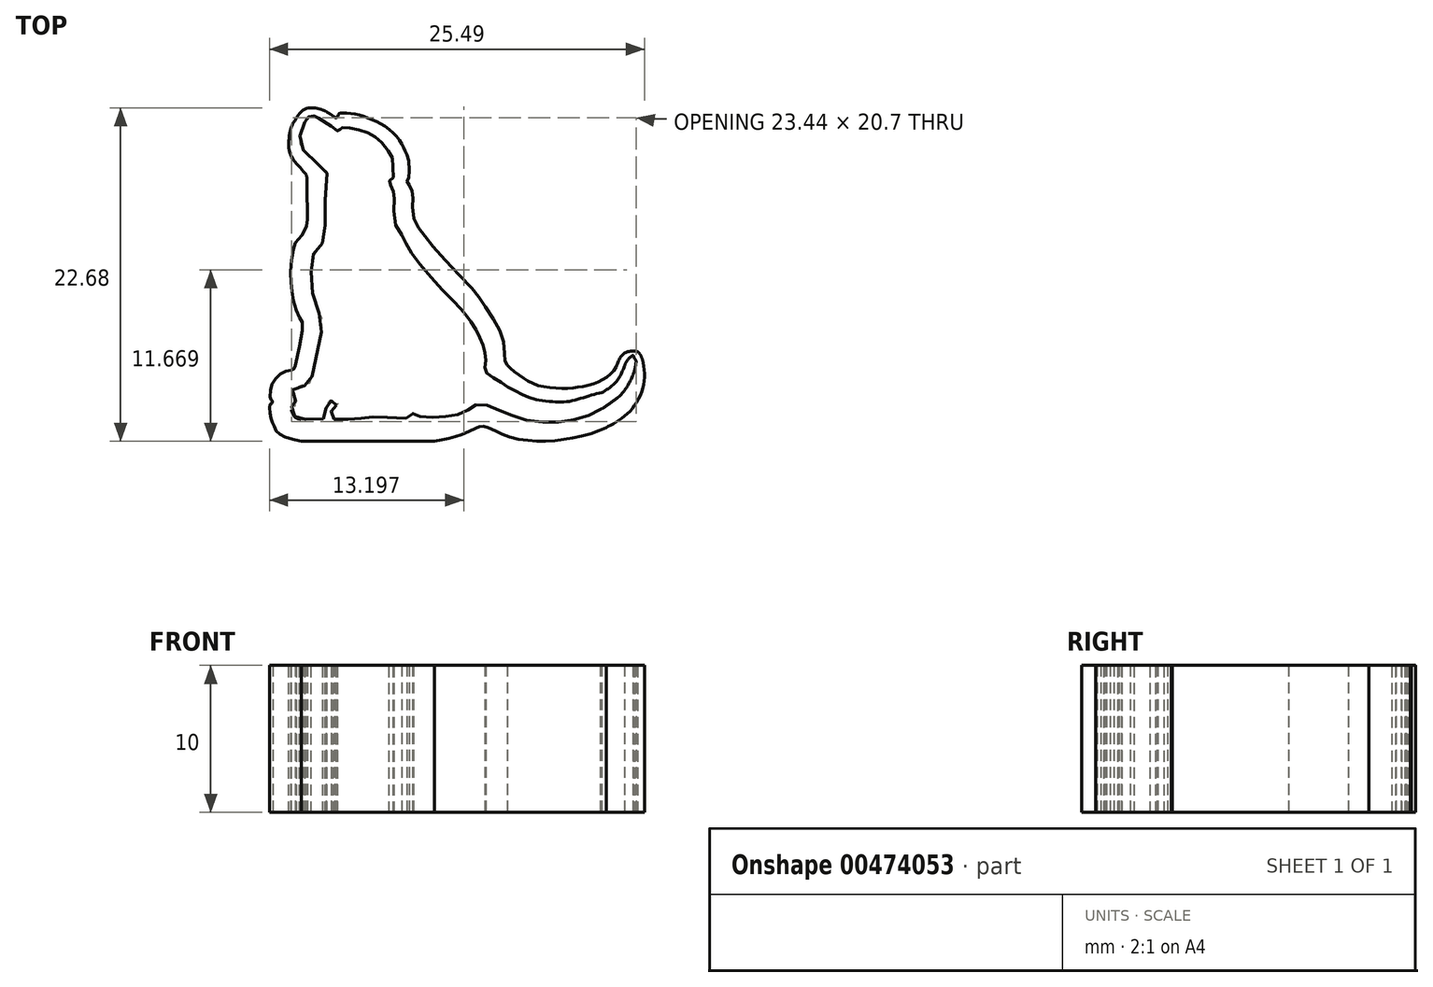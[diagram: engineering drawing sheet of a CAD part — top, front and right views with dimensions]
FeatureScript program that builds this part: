
annotation { "Feature Type Name" : "Feature", "Feature Type Description" : "" }
export const myFeature = defineFeature(function(context is Context, id is Id, definition is map)
    precondition{}
    {
        {
            var Q0;
            Q0=qCreatedBy(makeId("Top.planeOp"),FACE);
            var sketch = newSketch(context, id + "F0", { "sketchPlane" : qUnion([Q0])});
            skFitSpline(sketch, "E0", {"points": [v(-18.64, 26.8) * mm, v(-17.67, 25.17) * mm, v(-15, 22.17) * mm, v(-14.18, 21.25) * mm, v(-13.45, 20.1) * mm, v(-13.07, 19.16) * mm, v(-12.93, 18.19) * mm, v(-12.96, 17.55) * mm, v(-12.13, 16.92) * mm, v(-11.21, 16.35) * mm, v(-10.31, 15.9) * mm, v(-9.5, 15.6) * mm, v(-8.22, 15.45) * mm, v(-7.3, 15.48) * mm, v(-6.28, 15.74) * mm, v(-5.41, 16) * mm, v(-4.68, 16.04) * mm, v(-4.2, 15.74) * mm, v(-4.11, 15.31) * mm, v(-4.47, 14.84) * mm], "startDerivative": vector(10.05, -20.8) * mm, "endDerivative": vector(-11.78, -11.66) * mm});
            skFitSpline(sketch, "E1", {"points": [v(-9.5, 15.6) * mm, v(-8.72, 15.47) * mm, v(-7.72, 15.38) * mm, v(-6.88, 15.45) * mm, v(-6.21, 15.6) * mm, v(-5.62, 15.8) * mm, v(-5.06, 15.91) * mm, v(-4.74, 15.84) * mm, v(-4.58, 15.6) * mm, v(-4.64, 15.45) * mm, v(-4.81, 15.22) * mm, v(-5.13, 14.94) * mm, v(-5.65, 14.65) * mm, v(-6.3, 14.4) * mm, v(-7.1, 14.19) * mm, v(-7.82, 14.1) * mm, v(-8.74, 14.07) * mm, v(-9.5, 14.11) * mm, v(-10.51, 14.3) * mm, v(-11.1, 14.5) * mm, v(-11.64, 14.71) * mm, v(-12.33, 15) * mm, v(-12.8, 15.2) * mm, v(-13.18, 15.28) * mm, v(-13.65, 15.21) * mm, v(-13.89, 15.06) * mm, v(-14.13, 14.88) * mm, v(-14.44, 14.71) * mm, v(-14.94, 14.56) * mm, v(-15.47, 14.48) * mm, v(-16.02, 14.43) * mm, v(-16.6, 14.4) * mm, v(-17.18, 14.43) * mm, v(-17.55, 14.5) * mm, v(-17.68, 14.65) * mm, v(-17.88, 14.66) * mm, v(-17.96, 14.47) * mm, v(-18.17, 14.36) * mm, v(-19.22, 14.37) * mm, v(-20.18, 14.41) * mm, v(-20.7, 14.43) * mm, v(-21.2, 14.36) * mm, v(-21.69, 14.3) * mm, v(-22.28, 14.26) * mm, v(-23, 14.28) * mm, v(-23.35, 14.32) * mm, v(-23.43, 14.63) * mm, v(-23.4, 14.91) * mm, v(-23.24, 15.12) * mm, v(-23.07, 15.23) * mm], "startDerivative": vector(23.7, -7.27) * mm, "endDerivative": vector(13.55, 6.78) * mm});
            skFitSpline(sketch, "E2", {"points": [v(-18.64, 26.8) * mm, v(-19.13, 27.71) * mm, v(-19.15, 29.17) * mm, v(-19.16, 29.6) * mm, v(-19.26, 29.95) * mm, v(-19.43, 30.25) * mm, v(-19.49, 30.38) * mm, v(-19.43, 30.5) * mm, v(-19.26, 30.6) * mm, v(-19.2, 31.05) * mm, v(-19.26, 31.93) * mm, v(-19.33, 32.16) * mm, v(-19.82, 32.9) * mm, v(-20.2, 33.28) * mm, v(-20.67, 33.61) * mm, v(-21.2, 33.84) * mm, v(-21.83, 34.02) * mm, v(-22.38, 34.1) * mm, v(-22.69, 34.1) * mm, v(-22.78, 34.08) * mm, v(-22.83, 34) * mm, v(-22.85, 33.9) * mm, v(-22.92, 33.87) * mm, v(-23.02, 33.88) * mm, v(-23.16, 33.98) * mm, v(-24.31, 34.78) * mm, v(-24.49, 34.85) * mm, v(-24.67, 34.9) * mm, v(-24.86, 34.88) * mm, v(-25.01, 34.78) * mm, v(-25.2, 34.53) * mm, v(-25.25, 34.43) * mm, v(-25.24, 34.3) * mm, v(-25.23, 34.18) * mm], "startDerivative": vector(-11.38, 14.65) * mm, "endDerivative": vector(0.42, -6.75) * mm});
            skFitSpline(sketch, "E3", {"points": [v(-25.2, 34.53) * mm, v(-25.43, 34.12) * mm, v(-25.55, 33.7) * mm, v(-25.57, 33.14) * mm, v(-25.47, 32.8) * mm, v(-25.05, 32.28) * mm, v(-24.37, 31.64) * mm, v(-23.88, 31.24) * mm, v(-23.75, 31.13) * mm, v(-23.71, 30.96) * mm, v(-23.81, 29.43) * mm, v(-23.83, 27.82) * mm, v(-23.86, 27.12) * mm, v(-23.99, 26.36) * mm, v(-24.2, 26) * mm, v(-24.5, 25.67) * mm, v(-24.72, 25.34) * mm, v(-24.79, 24.67) * mm, v(-24.75, 23.66) * mm, v(-24.68, 22.74) * mm, v(-24.45, 21.84) * mm, v(-24.06, 21.1) * mm, v(-24.02, 20.72) * mm, v(-24.75, 17.1) * mm, v(-24.88, 16.75) * mm, v(-25.02, 16.6) * mm, v(-25.46, 16.55) * mm, v(-25.84, 16.43) * mm, v(-26.05, 16.28) * mm, v(-26.1, 15.69) * mm, v(-25.95, 15.55) * mm, v(-25.8, 15.44) * mm, v(-25.8, 15.29) * mm, v(-25.91, 15.22) * mm, v(-26.08, 15.2) * mm, v(-26.14, 14.98) * mm, v(-26.1, 14.74) * mm, v(-25.97, 14.52) * mm, v(-25.8, 14.35) * mm, v(-25.63, 14.29) * mm, v(-25.36, 14.27) * mm, v(-24.45, 14.27) * mm, v(-24.02, 14.29) * mm, v(-23.87, 14.38) * mm, v(-23.84, 14.72) * mm, v(-23.78, 15.01) * mm, v(-23.63, 15.25) * mm, v(-23.6, 15.46) * mm, v(-23.52, 15.52) * mm, v(-23.34, 15.52) * mm, v(-23.16, 15.45) * mm, v(-22.98, 15.35) * mm, v(-23.07, 15.23) * mm], "startDerivative": vector(-12.69, -20.47) * mm, "endDerivative": vector(-12.96, -11.1) * mm});
            skFitSpline(sketch, "E4", {"points": [v(-23.08, 16.7) * mm, v(-21.94, 19.17) * mm, v(-21.85, 19.47) * mm, v(-21.79, 19.58) * mm, v(-21.64, 19.6) * mm, v(-21.56, 19.53) * mm, v(-21.54, 19.42) * mm, v(-21.46, 19.35) * mm, v(-21.26, 19.2) * mm, v(-21.06, 19.1) * mm, v(-20.96, 19.02) * mm, v(-20.97, 18.84) * mm, v(-21.11, 18.68) * mm, v(-21.16, 18.5) * mm, v(-21.17, 18.18) * mm, v(-21.1, 17.9) * mm, v(-20.94, 17.57) * mm, v(-20.66, 17.12) * mm, v(-20.63, 16.86) * mm, v(-20.8, 16.71) * mm, v(-21.1, 16.62) * mm, v(-21.6, 16.57) * mm, v(-22.32, 16.56) * mm, v(-22.93, 16.5) * mm, v(-23.08, 16.53) * mm, v(-23.13, 16.58) * mm, v(-23.08, 16.7) * mm]});
            skFitSpline(sketch, "E5", {"points": [v(-21.86, 15.57) * mm, v(-19.82, 15.8) * mm, v(-19.69, 15.8) * mm, v(-19.62, 15.6) * mm, v(-19.68, 15.5) * mm, v(-20.03, 15.34) * mm, v(-20.57, 15.23) * mm, v(-21.23, 15.2) * mm, v(-21.7, 15.28) * mm, v(-21.84, 15.34) * mm], "startDerivative": vector(10.76, 1.04) * mm, "endDerivative": vector(-1.73, 0.9) * mm});
            skFitSpline(sketch, "E6", {"points": [v(-21.84, 15.34) * mm, v(-21.88, 15.44) * mm, v(-21.86, 15.57) * mm], "startDerivative": vector(-0.1, 0.21) * mm, "endDerivative": vector(0.07, 0.25) * mm});
            skPoint(sketch, "E7.1.internal.orphan", {"position": v(-24.41, 31.05) * mm});
            skPoint(sketch, "E8.7.internal.snap0", {"position": v(-11.42, 13.4) * mm});
            skPoint(sketch, "E8.8.internal.snap0", {"position": v(-11.42, 13.45) * mm});
            skFitSpline(sketch, "E9.trimOffspring", {"points": [v(-11.33, 13.53) * mm, v(-12.83, 14.23) * mm, v(-13.03, 14.3) * mm, v(-13.4, 14.32) * mm, v(-13.63, 14.24) * mm, v(-14.53, 13.84) * mm, v(-15.5, 13.53) * mm, v(-18.01, 13.4) * mm, v(-24.51, 13.45) * mm, v(-26.14, 14.16) * mm], "startDerivative": vector(-14.88, 6.54) * mm, "endDerivative": vector(-9.16, 7.25) * mm});
            skFitSpline(sketch, "E10.trimOffspring", {"points": [v(-25.27, 17.31) * mm, v(-25.4, 17.12) * mm, v(-25.87, 17.05) * mm, v(-26.28, 16.9) * mm, v(-26.59, 16.65) * mm, v(-26.82, 16.2) * mm, v(-26.85, 15.72) * mm, v(-26.81, 15.56) * mm, v(-26.7, 15.48) * mm, v(-26.7, 15.43) * mm, v(-26.72, 15.35) * mm, v(-26.78, 15.29) * mm, v(-26.81, 15.27) * mm, v(-26.83, 15.23) * mm, v(-26.84, 15.17) * mm, v(-26.79, 14.82) * mm, v(-26.75, 14.37) * mm, v(-26.31, 13.9) * mm, v(-24.51, 13.45) * mm], "startDerivative": vector(-1.67, -4.49) * mm, "endDerivative": vector(14.6, -2.5) * mm});
            skFitSpline(sketch, "E11", {"points": [v(-6.48, 17.1) * mm, v(-7.36, 16.99) * mm, v(-8.18, 16.99) * mm, v(-9.04, 17.07) * mm, v(-9.92, 17.26) * mm, v(-10.74, 17.6) * mm, v(-11.45, 17.93) * mm, v(-11.59, 18.15) * mm, v(-11.63, 18.41) * mm, v(-11.7, 19.47) * mm, v(-12.19, 20.74) * mm, v(-13.2, 22.3) * mm, v(-13.91, 23.21) * mm, v(-16.3, 25.78) * mm, v(-17.26, 26.98) * mm, v(-17.78, 27.85) * mm, v(-17.88, 29.02) * mm, v(-17.86, 29.53) * mm, v(-18.02, 30.04) * mm, v(-18.2, 30.28) * mm, v(-18.27, 30.42) * mm, v(-18.25, 30.57) * mm, v(-18.17, 30.66) * mm, v(-18.13, 31.07) * mm, v(-18.18, 31.92) * mm, v(-18.28, 32.28) * mm, v(-18.85, 33.1) * mm, v(-19.38, 33.72) * mm, v(-20.14, 34.24) * mm, v(-20.86, 34.57) * mm, v(-21.64, 34.79) * mm, v(-22.34, 34.89) * mm, v(-22.74, 34.9) * mm, v(-22.87, 34.85) * mm, v(-22.9, 34.77) * mm, v(-22.92, 34.69) * mm, v(-22.94, 34.61) * mm, v(-23.03, 34.57) * mm, v(-23.1, 34.57) * mm, v(-23.2, 34.63) * mm, v(-23.38, 34.79) * mm], "startDerivative": vector(-28.78, -4.16) * mm, "endDerivative": vector(-12.37, 11.09) * mm});
            skFitSpline(sketch, "E12", {"points": [v(-18.28, 32.28) * mm, v(-18.57, 32.86) * mm, v(-19, 33.53) * mm, v(-19.88, 34.26) * mm, v(-20.7, 34.66) * mm, v(-21.58, 34.97) * mm, v(-22.33, 35.08) * mm, v(-22.76, 35.1) * mm, v(-22.88, 35.07) * mm, v(-22.95, 34.96) * mm, v(-23, 34.85) * mm, v(-23.04, 34.78) * mm, v(-23.12, 34.77) * mm, v(-23.16, 34.77) * mm, v(-23.22, 34.84) * mm, v(-23.3, 34.9) * mm, v(-23.53, 35.07) * mm], "startDerivative": vector(-3.23, 6.6) * mm, "endDerivative": vector(-4.35, 3.68) * mm});
            skFitSpline(sketch, "E13", {"points": [v(-23.04, 34.78) * mm, v(-23.06, 34.77) * mm, v(-23.1, 34.77) * mm, v(-23.14, 34.79) * mm, v(-23.4, 34.97) * mm, v(-23.76, 35.18) * mm, v(-24.11, 35.43) * mm, v(-24.54, 35.57) * mm, v(-24.95, 35.59) * mm, v(-25.4, 35.53) * mm, v(-25.8, 35.28) * mm, v(-26.19, 34.91) * mm, v(-26.45, 34.47) * mm, v(-26.72, 33.71) * mm, v(-26.75, 32.98) * mm, v(-26.57, 32.2) * mm, v(-26.07, 31.53) * mm, v(-25.4, 31) * mm, v(-25.12, 30.88) * mm, v(-25.08, 30.74) * mm, v(-25.07, 30.57) * mm, v(-25.07, 29.48) * mm, v(-25.05, 27.86) * mm, v(-25.12, 27.36) * mm, v(-25.28, 27.01) * mm, v(-25.4, 26.8) * mm, v(-25.6, 26.59) * mm, v(-25.8, 26.4) * mm, v(-25.95, 25.99) * mm, v(-26.1, 25.28) * mm, v(-26.17, 24.68) * mm, v(-26.15, 23.63) * mm, v(-26.07, 22.7) * mm, v(-25.8, 21.62) * mm, v(-25.47, 21.02) * mm, v(-25.37, 20.78) * mm, v(-25.88, 17.9) * mm], "startDerivative": vector(-3.52, -1.33) * mm, "endDerivative": vector(-12.4, -56.43) * mm});
            skFitSpline(sketch, "E14", {"points": [v(-25.88, 17.9) * mm, v(-25.93, 17.73) * mm, v(-26.03, 17.63) * mm, v(-26.34, 17.56) * mm, v(-26.8, 17.41) * mm, v(-27.3, 16.88) * mm, v(-27.55, 16.35) * mm, v(-27.58, 15.74) * mm, v(-27.54, 15.61) * mm, v(-27.45, 15.55) * mm, v(-27.42, 15.51) * mm, v(-27.42, 15.42) * mm, v(-27.48, 15.34) * mm, v(-27.53, 15.31) * mm, v(-27.6, 15.28) * mm, v(-27.62, 15.2) * mm, v(-27.6, 14.84) * mm, v(-27.54, 14.37) * mm, v(-27.46, 14.1) * mm, v(-27.33, 13.82) * mm, v(-27.18, 13.48) * mm, v(-26.9, 13.22) * mm, v(-26.42, 13.01) * mm, v(-26.1, 12.92) * mm, v(-25.44, 12.77) * mm], "startDerivative": vector(-1.3, -5.64) * mm, "endDerivative": vector(11.14, -2.6) * mm});
            skLineSegment(sketch, "E15", {"start": v(-25.44, 12.77) * mm, "end": v(-16.4, 12.77) * mm});
            skFitSpline(sketch, "E16", {"points": [v(-16.4, 12.77) * mm, v(-15.63, 12.92) * mm, v(-15, 13.08) * mm, v(-14.33, 13.31) * mm, v(-13.57, 13.67) * mm, v(-13.43, 13.74) * mm, v(-13.13, 13.8) * mm, v(-12.95, 13.77) * mm, v(-12.2, 13.45) * mm, v(-11.48, 13.1) * mm, v(-10.27, 12.85) * mm, v(-9.14, 12.77) * mm, v(-7.98, 12.84) * mm, v(-6.82, 13.04) * mm, v(-5.6, 13.35) * mm, v(-4.74, 13.7) * mm, v(-4.16, 13.95) * mm, v(-3.3, 14.47) * mm, v(-2.28, 15.31) * mm], "startDerivative": vector(14.64, 2.55) * mm, "endDerivative": vector(13.76, 11.69) * mm});
            skFitSpline(sketch, "E17.trimOffspring", {"points": [v(-23.04, 34.78) * mm, v(-23.06, 34.77) * mm, v(-23.1, 34.77) * mm, v(-23.14, 34.79) * mm, v(-23.4, 34.97) * mm, v(-23.76, 35.18) * mm, v(-24.11, 35.43) * mm, v(-24.54, 35.57) * mm, v(-24.95, 35.59) * mm, v(-25.4, 35.53) * mm, v(-25.8, 35.28) * mm, v(-26.19, 34.91) * mm, v(-26.45, 34.47) * mm, v(-26.72, 33.71) * mm, v(-26.75, 32.98) * mm, v(-26.57, 32.2) * mm, v(-26.07, 31.53) * mm, v(-25.4, 31) * mm, v(-25.12, 30.88) * mm, v(-25.08, 30.74) * mm, v(-25.07, 30.57) * mm, v(-25.07, 29.48) * mm, v(-25.05, 27.86) * mm, v(-25.12, 27.36) * mm, v(-25.28, 27.01) * mm, v(-25.4, 26.8) * mm, v(-25.6, 26.59) * mm, v(-25.8, 26.4) * mm, v(-25.95, 25.99) * mm, v(-26.1, 25.28) * mm, v(-26.17, 24.68) * mm, v(-26.15, 23.63) * mm, v(-26.07, 22.7) * mm, v(-25.8, 21.62) * mm, v(-25.47, 21.02) * mm, v(-25.37, 20.78) * mm, v(-25.88, 17.9) * mm], "startDerivative": vector(-3.52, -1.33) * mm, "endDerivative": vector(-12.4, -56.43) * mm});
            skFitSpline(sketch, "E18", {"points": [v(-26.15, 34.12) * mm, v(-26.08, 34.28) * mm, v(-25.97, 34.48) * mm, v(-25.83, 34.71) * mm, v(-25.67, 34.93) * mm, v(-25.43, 35.2) * mm, v(-25.21, 35.36) * mm, v(-24.98, 35.44) * mm, v(-24.8, 35.45) * mm, v(-24.63, 35.44) * mm, v(-24.43, 35.41) * mm, v(-24.2, 35.35) * mm, v(-23.93, 35.27) * mm, v(-23.76, 35.18) * mm], "startDerivative": vector(1.03, 2.42) * mm, "endDerivative": vector(3.44, -1.92) * mm});
            skFitSpline(sketch, "E19", {"points": [v(-25.12, 30.88) * mm, v(-25.24, 31.05) * mm, v(-25.58, 31.42) * mm, v(-26.06, 32.01) * mm, v(-26.3, 32.58) * mm, v(-26.32, 33.06) * mm, v(-26.25, 33.67) * mm, v(-26.15, 34.12) * mm], "startDerivative": vector(-1.17, 1.7) * mm, "endDerivative": vector(0.8, 3.11) * mm});
            skLineSegment(sketch, "E20", {"start": v(-5.13, 14.94) * mm, "end": v(-4.98, 14.75) * mm});
            skLineSegment(sketch, "E21", {"start": v(-5.13, 14.94) * mm, "end": v(-5.25, 15.08) * mm});
            skLineSegment(sketch, "E22", {"start": v(-11.45, 17.93) * mm, "end": v(-11.27, 18.13) * mm});
            skLineSegment(sketch, "E23", {"start": v(-11.45, 17.93) * mm, "end": v(-11.67, 17.7) * mm});
            skFitSpline(sketch, "E24", {"points": [v(-11.45, 17.93) * mm, v(-11.1, 17.6) * mm, v(-10.53, 17.18) * mm, v(-9.97, 16.83) * mm, v(-9.33, 16.55) * mm, v(-8.54, 16.42) * mm, v(-7.67, 16.35) * mm, v(-6.99, 16.4) * mm, v(-6.4, 16.48) * mm, v(-5.7, 16.64) * mm, v(-5.21, 16.84) * mm, v(-4.75, 17.1) * mm, v(-4.32, 17.46) * mm, v(-4.06, 17.83) * mm, v(-3.85, 18.33) * mm, v(-3.62, 18.66) * mm, v(-3.34, 18.84) * mm, v(-3.05, 18.9) * mm, v(-2.79, 18.9) * mm, v(-2.57, 18.85) * mm, v(-2.45, 18.6) * mm, v(-2.42, 18.16) * mm, v(-2.45, 17.6) * mm, v(-2.53, 17.03) * mm], "startDerivative": vector(7.84, -7.71) * mm, "endDerivative": vector(-1.96, -12.26) * mm});
            skFitSpline(sketch, "E25", {"points": [v(-5.62, 15.8) * mm, v(-5.17, 16) * mm, v(-4.74, 16.25) * mm, v(-4.32, 16.56) * mm, v(-3.94, 16.96) * mm, v(-3.65, 17.49) * mm, v(-3.49, 17.88) * mm, v(-3.31, 18.22) * mm, v(-3.18, 18.36) * mm, v(-3.03, 18.4) * mm, v(-2.85, 18.4) * mm, v(-2.76, 18.33) * mm, v(-2.71, 18.24) * mm, v(-2.71, 18.09) * mm, v(-2.73, 17.96) * mm, v(-2.8, 17.76) * mm], "startDerivative": vector(5.23, 2.04) * mm, "endDerivative": vector(-1.4, -3.71) * mm});
            skFitSpline(sketch, "E26", {"points": [v(-5.13, 14.94) * mm, v(-4.9, 15.07) * mm, v(-4.56, 15.28) * mm, v(-4.24, 15.52) * mm, v(-3.83, 15.85) * mm, v(-3.45, 16.28) * mm, v(-3.16, 16.75) * mm, v(-2.9, 17.3) * mm, v(-2.73, 17.96) * mm], "startDerivative": vector(2.45, 1.27) * mm, "endDerivative": vector(0.98, 4.52) * mm});
            skLineSegment(sketch, "E27", {"start": v(-3.49, 17.88) * mm, "end": v(-3.62, 17.94) * mm});
            skLineSegment(sketch, "E28", {"start": v(-3.49, 17.88) * mm, "end": v(-3.35, 17.82) * mm});
            skLineSegment(sketch, "E29", {"start": v(-2.9, 17.3) * mm, "end": v(-2.82, 17.28) * mm});
            skLineSegment(sketch, "E30", {"start": v(-2.9, 17.3) * mm, "end": v(-3, 17.34) * mm});
            skFitSpline(sketch, "E31", {"points": [v(-3.49, 17.88) * mm, v(-3.42, 18.05) * mm, v(-3.36, 18.18) * mm, v(-3.22, 18.37) * mm, v(-3.07, 18.51) * mm, v(-2.9, 18.61) * mm], "startDerivative": vector(0.32, 0.9) * mm, "endDerivative": vector(0.83, 0.47) * mm});
            skFitSpline(sketch, "E32", {"points": [v(-2.9, 17.3) * mm, v(-2.84, 17.49) * mm, v(-2.78, 17.69) * mm, v(-2.75, 17.92) * mm, v(-2.74, 18.1) * mm, v(-2.75, 18.2) * mm, v(-2.8, 18.39) * mm, v(-2.86, 18.54) * mm, v(-2.9, 18.61) * mm], "startDerivative": vector(0.45, 1.34) * mm, "endDerivative": vector(-0.44, 0.75) * mm});
            skFitSpline(sketch, "E33", {"points": [v(-4.74, 13.7) * mm, v(-4.41, 13.87) * mm, v(-3.93, 14.16) * mm, v(-3.35, 14.58) * mm, v(-2.86, 15.13) * mm, v(-2.43, 15.85) * mm, v(-2.2, 16.6) * mm, v(-2.13, 17.4) * mm, v(-2.22, 18.12) * mm, v(-2.34, 18.51) * mm, v(-2.45, 18.71) * mm, v(-2.57, 18.85) * mm], "startDerivative": vector(4.17, 2.2) * mm, "endDerivative": vector(-2.37, 2.44) * mm});
            skLineSegment(sketch, "E34", {"start": v(-4.06, 17.83) * mm, "end": v(-4.26, 17.92) * mm});
            skLineSegment(sketch, "E35", {"start": v(-4.06, 17.83) * mm, "end": v(-3.86, 17.74) * mm});
            skLineSegment(sketch, "E36", {"start": v(-2.22, 18.12) * mm, "end": v(-2, 18.12) * mm});
            skLineSegment(sketch, "E37", {"start": v(-2.22, 18.12) * mm, "end": v(-2.33, 18.12) * mm});
            skPoint(sketch, "E38.1.internal.snap0", {"position": v(-3.96, 17.78) * mm});
            skFitSpline(sketch, "E38", {"points": [v(-4.06, 17.83) * mm, v(-3.96, 18.14) * mm, v(-3.79, 18.6) * mm, v(-3.53, 19.01) * mm, v(-3.18, 19.32) * mm, v(-2.85, 19.54) * mm], "startDerivative": vector(0.54, 1.72) * mm, "endDerivative": vector(1.7, 1.08) * mm});
            skFitSpline(sketch, "E39", {"points": [v(-2.22, 18.12) * mm, v(-2.26, 18.35) * mm, v(-2.33, 18.66) * mm, v(-2.41, 18.99) * mm, v(-2.53, 19.3) * mm, v(-2.66, 19.48) * mm, v(-2.7, 19.53) * mm, v(-2.79, 19.56) * mm, v(-2.85, 19.54) * mm], "startDerivative": vector(-0.23, 1.58) * mm, "endDerivative": vector(-0.75, -0.43) * mm});
            skSolve(sketch);
        }
        {
            var Q0;
            Q0=makeQuery(id+"F0.imprint","IMPRINT",FACE,{"disambiguationData":[TD([[makeQuery(id+"F0.imprint","IMPRINT",EDGE,{"derivedFrom":sQuery(id+"F0.wireOp",EDGE,"E0")}),1.0]])]});
            extrude(context, id + "F1", {"entities" : qUnion([Q0]), "depth" : 10 * mm});
        }
    });
